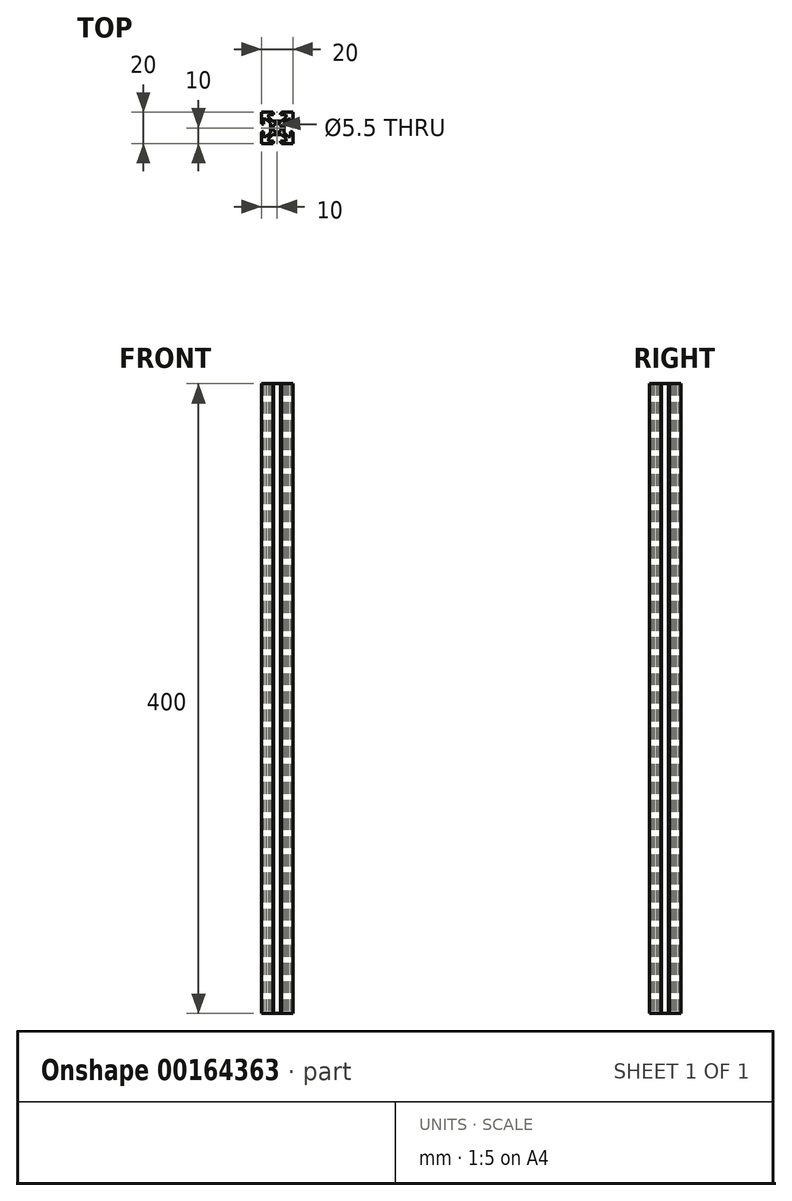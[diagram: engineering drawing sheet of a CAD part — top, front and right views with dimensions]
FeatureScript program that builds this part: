
annotation { "Feature Type Name" : "Feature", "Feature Type Description" : "" }
export const myFeature = defineFeature(function(context is Context, id is Id, definition is map)
    precondition{}
    {
        {
            var Q0;
            Q0=qCreatedBy(makeId("Top.planeOp"),FACE);
            var sketch = newSketch(context, id + "F0", { "sketchPlane" : qUnion([Q0])});
            skLineSegment(sketch, "E0.bottom", {"start": v(0, 0) * mm, "end": v(7.25, 0) * mm});
            skLineSegment(sketch, "E0.top", {"start": v(0, 20) * mm, "end": v(7.25, 20) * mm});
            skLineSegment(sketch, "E0.left", {"start": v(0, 0) * mm, "end": v(0, 7.25) * mm});
            skLineSegment(sketch, "E0.right", {"start": v(20, 0) * mm, "end": v(20, 7.25) * mm});
            skCircle(sketch, "E1", {"center": v(10, 10) * mm, "radius": 2.75 * mm});
            skLineSegment(sketch, "E2", {"start": v(7.25, 20) * mm, "end": v(7.25, 19.5) * mm});
            skLineSegment(sketch, "E3", {"start": v(7.25, 19.5) * mm, "end": v(7.75, 19.5) * mm});
            skLineSegment(sketch, "E4", {"start": v(7.75, 19.5) * mm, "end": v(7.75, 18.5) * mm});
            skLineSegment(sketch, "E5", {"start": v(7.75, 18.5) * mm, "end": v(4.5, 18.5) * mm});
            skLineSegment(sketch, "E6", {"start": v(4.5, 18.5) * mm, "end": v(4.5, 16.97) * mm});
            skLineSegment(sketch, "E7", {"start": v(4.5, 16.97) * mm, "end": v(7.11, 14.3) * mm});
            skLineSegment(sketch, "E8", {"start": v(10, 20) * mm, "end": v(10, 0) * mm, "construction": true});
            skLineSegment(sketch, "E9", {"start": v(7.11, 14.3) * mm, "end": v(10, 14.3) * mm});
            skLineSegment(sketch, "E10.MirrorCS", {"start": v(12.75, 19.5) * mm, "end": v(12.25, 19.5) * mm});
            skLineSegment(sketch, "E11.MirrorCS", {"start": v(12.75, 20) * mm, "end": v(12.75, 19.5) * mm});
            skLineSegment(sketch, "E12.MirrorCS", {"start": v(12.25, 19.5) * mm, "end": v(12.25, 18.5) * mm});
            skLineSegment(sketch, "E13.MirrorCS", {"start": v(15.5, 16.97) * mm, "end": v(12.89, 14.3) * mm});
            skLineSegment(sketch, "E14.MirrorCS", {"start": v(15.5, 18.5) * mm, "end": v(15.5, 16.97) * mm});
            skLineSegment(sketch, "E15.MirrorCS", {"start": v(12.25, 18.5) * mm, "end": v(15.5, 18.5) * mm});
            skLineSegment(sketch, "E16.MirrorCS", {"start": v(12.89, 14.3) * mm, "end": v(10, 14.3) * mm});
            skLineSegment(sketch, "E17.1.0", {"start": v(1.5, 15.5) * mm, "end": v(3.03, 15.5) * mm});
            skLineSegment(sketch, "E17.1.1", {"start": v(5.7, 12.89) * mm, "end": v(5.7, 10) * mm});
            skLineSegment(sketch, "E17.1.2", {"start": v(1.5, 4.5) * mm, "end": v(3.03, 4.5) * mm});
            skLineSegment(sketch, "E17.1.3", {"start": v(5.7, 7.11) * mm, "end": v(5.7, 10) * mm});
            skLineSegment(sketch, "E17.1.4", {"start": v(1.5, 7.75) * mm, "end": v(1.5, 4.5) * mm});
            skLineSegment(sketch, "E17.1.5", {"start": v(3.03, 4.5) * mm, "end": v(5.7, 7.11) * mm});
            skLineSegment(sketch, "E17.1.6", {"start": v(1.5, 12.25) * mm, "end": v(1.5, 15.5) * mm});
            skLineSegment(sketch, "E17.1.7", {"start": v(3.03, 15.5) * mm, "end": v(5.7, 12.89) * mm});
            skLineSegment(sketch, "E17.1.8", {"start": v(0.5, 7.75) * mm, "end": v(1.5, 7.75) * mm});
            skLineSegment(sketch, "E17.1.9", {"start": v(0.5, 12.25) * mm, "end": v(1.5, 12.25) * mm});
            skLineSegment(sketch, "E17.1.10", {"start": v(0.5, 12.75) * mm, "end": v(0.5, 12.25) * mm});
            skLineSegment(sketch, "E17.1.11", {"start": v(0, 12.75) * mm, "end": v(0.5, 12.75) * mm});
            skLineSegment(sketch, "E17.1.12", {"start": v(0.5, 7.25) * mm, "end": v(0.5, 7.75) * mm});
            skLineSegment(sketch, "E17.1.13", {"start": v(0, 7.25) * mm, "end": v(0.5, 7.25) * mm});
            skLineSegment(sketch, "E17.2.0", {"start": v(4.5, 1.5) * mm, "end": v(4.5, 3.03) * mm});
            skLineSegment(sketch, "E17.2.1", {"start": v(7.11, 5.7) * mm, "end": v(10, 5.7) * mm});
            skLineSegment(sketch, "E17.2.2", {"start": v(15.5, 1.5) * mm, "end": v(15.5, 3.03) * mm});
            skLineSegment(sketch, "E17.2.3", {"start": v(12.89, 5.7) * mm, "end": v(10, 5.7) * mm});
            skLineSegment(sketch, "E17.2.4", {"start": v(12.25, 1.5) * mm, "end": v(15.5, 1.5) * mm});
            skLineSegment(sketch, "E17.2.5", {"start": v(15.5, 3.03) * mm, "end": v(12.89, 5.7) * mm});
            skLineSegment(sketch, "E17.2.6", {"start": v(7.75, 1.5) * mm, "end": v(4.5, 1.5) * mm});
            skLineSegment(sketch, "E17.2.7", {"start": v(4.5, 3.03) * mm, "end": v(7.11, 5.7) * mm});
            skLineSegment(sketch, "E17.2.8", {"start": v(12.25, 0.5) * mm, "end": v(12.25, 1.5) * mm});
            skLineSegment(sketch, "E17.2.9", {"start": v(7.75, 0.5) * mm, "end": v(7.75, 1.5) * mm});
            skLineSegment(sketch, "E17.2.10", {"start": v(7.25, 0.5) * mm, "end": v(7.75, 0.5) * mm});
            skLineSegment(sketch, "E17.2.11", {"start": v(7.25, 0) * mm, "end": v(7.25, 0.5) * mm});
            skLineSegment(sketch, "E17.2.12", {"start": v(12.75, 0.5) * mm, "end": v(12.25, 0.5) * mm});
            skLineSegment(sketch, "E17.2.13", {"start": v(12.75, 0) * mm, "end": v(12.75, 0.5) * mm});
            skLineSegment(sketch, "E17.3.0", {"start": v(18.5, 4.5) * mm, "end": v(16.97, 4.5) * mm});
            skLineSegment(sketch, "E17.3.1", {"start": v(14.3, 7.11) * mm, "end": v(14.3, 10) * mm});
            skLineSegment(sketch, "E17.3.2", {"start": v(18.5, 15.5) * mm, "end": v(16.97, 15.5) * mm});
            skLineSegment(sketch, "E17.3.3", {"start": v(14.3, 12.89) * mm, "end": v(14.3, 10) * mm});
            skLineSegment(sketch, "E17.3.4", {"start": v(18.5, 12.25) * mm, "end": v(18.5, 15.5) * mm});
            skLineSegment(sketch, "E17.3.5", {"start": v(16.97, 15.5) * mm, "end": v(14.3, 12.89) * mm});
            skLineSegment(sketch, "E17.3.6", {"start": v(18.5, 7.75) * mm, "end": v(18.5, 4.5) * mm});
            skLineSegment(sketch, "E17.3.7", {"start": v(16.97, 4.5) * mm, "end": v(14.3, 7.11) * mm});
            skLineSegment(sketch, "E17.3.8", {"start": v(19.5, 12.25) * mm, "end": v(18.5, 12.25) * mm});
            skLineSegment(sketch, "E17.3.9", {"start": v(19.5, 7.75) * mm, "end": v(18.5, 7.75) * mm});
            skLineSegment(sketch, "E17.3.10", {"start": v(19.5, 7.25) * mm, "end": v(19.5, 7.75) * mm});
            skLineSegment(sketch, "E17.3.11", {"start": v(20, 7.25) * mm, "end": v(19.5, 7.25) * mm});
            skLineSegment(sketch, "E17.3.12", {"start": v(19.5, 12.75) * mm, "end": v(19.5, 12.25) * mm});
            skLineSegment(sketch, "E17.3.13", {"start": v(20, 12.75) * mm, "end": v(19.5, 12.75) * mm});
            skLineSegment(sketch, "E18.trimOffspring", {"start": v(12.75, 20) * mm, "end": v(20, 20) * mm});
            skLineSegment(sketch, "E19.trimOffspring", {"start": v(0, 12.75) * mm, "end": v(0, 20) * mm});
            skLineSegment(sketch, "E20.trimOffspring", {"start": v(12.75, 0) * mm, "end": v(20, 0) * mm});
            skLineSegment(sketch, "E21.trimOffspring", {"start": v(20, 12.75) * mm, "end": v(20, 20) * mm});
            skSolve(sketch);
        }
        {
            var Q0;
            Q0=makeQuery(id+"F0.imprint","IMPRINT",FACE,{"disambiguationData":[TD([[makeQuery(id+"F0.imprint","IMPRINT",EDGE,{"derivedFrom":sQuery(id+"F0.wireOp",EDGE,"E0.bottom")}),1.0]])]});
            extrude(context, id + "F1", {"entities" : qUnion([Q0]), "depth" : 400 * mm});
        }
    });
